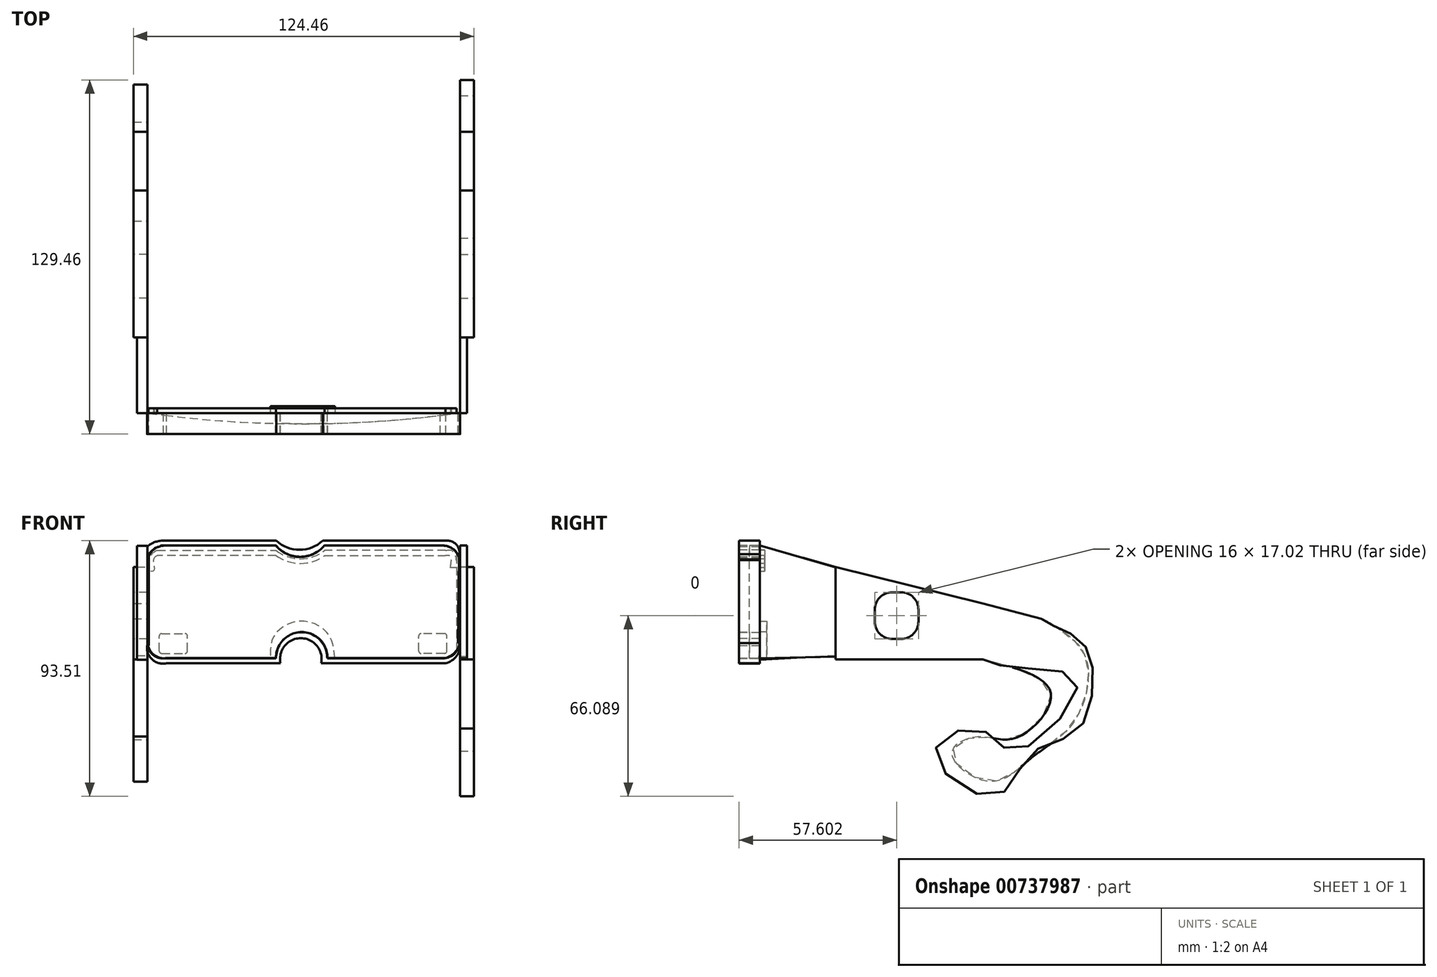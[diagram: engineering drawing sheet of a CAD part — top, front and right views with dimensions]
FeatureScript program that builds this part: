
annotation { "Feature Type Name" : "Feature", "Feature Type Description" : "" }
export const myFeature = defineFeature(function(context is Context, id is Id, definition is map)
    precondition{}
    {
        {
            var Q0;
            Q0=qCreatedBy(makeId("Front.planeOp"),FACE);
            var sketch = newSketch(context, id + "F0", { "sketchPlane" : qUnion([Q0])});
            skLineSegment(sketch, "E0", {"start": v(0, 0) * mm, "end": v(-56.1, 0) * mm});
            skLineSegment(sketch, "E1.left", {"start": v(-56.1, 21.29) * mm, "end": v(-56.1, -7.3) * mm});
            skLineSegment(sketch, "E1.right", {"start": v(58.2, 21.29) * mm, "end": v(58.2, -7.3) * mm});
            skArc(sketch, "E2", {"start": v(9.78, -13.65) * mm, "mid": v(0.38, -3.97) * mm, "end": v(-9.02, -13.65) * mm});
            skArc(sketch, "E3", {"start": v(-9.02, 27.64) * mm, "mid": v(-0.21, 23.55) * mm, "end": v(8.59, 27.64) * mm});
            skLineSegment(sketch, "E4", {"start": v(-9.02, 27.64) * mm, "end": v(-49.75, 27.64) * mm});
            skLineSegment(sketch, "E5", {"start": v(8.59, 27.64) * mm, "end": v(51.85, 27.64) * mm});
            skPoint(sketch, "E6.visualSharp", {"position": v(58.2, 27.64) * mm});
            skArc(sketch, "E6.filletArc", {"start": v(58.2, 21.29) * mm, "mid": v(56.34, 25.78) * mm, "end": v(51.85, 27.64) * mm});
            skPoint(sketch, "E7.visualSharp", {"position": v(-56.1, -13.65) * mm});
            skArc(sketch, "E7.filletArc", {"start": v(-56.1, -7.3) * mm, "mid": v(-54.24, -11.79) * mm, "end": v(-49.75, -13.65) * mm});
            skPoint(sketch, "E8.visualSharp", {"position": v(58.2, -13.65) * mm});
            skArc(sketch, "E8.filletArc", {"start": v(51.85, -13.65) * mm, "mid": v(56.34, -11.79) * mm, "end": v(58.2, -7.3) * mm});
            skPoint(sketch, "E9.visualSharp", {"position": v(-56.1, 27.64) * mm});
            skArc(sketch, "E9.filletArc", {"start": v(-49.75, 27.64) * mm, "mid": v(-54.24, 25.78) * mm, "end": v(-56.1, 21.29) * mm});
            skLineSegment(sketch, "E10", {"start": v(-49.75, -13.65) * mm, "end": v(-9.02, -13.65) * mm});
            skLineSegment(sketch, "E11", {"start": v(9.78, -13.65) * mm, "end": v(51.85, -13.65) * mm});
            skSolve(sketch);
        }
        {
            var Q0;
            Q0 = qSketchRegion(id + "F0", true);
            extrude(context, id + "F1", {"entities" : qUnion([Q0]), "depth" : 7.62 * mm, "offsetDistance" : 25.4 * mm});
        }
        {
            var Q0;
            Q0=makeQuery(id+"F1.opExtrude","SWEPT_FACE",FACE,{"disambiguationData":[OSD([sQuery(id+"F0.wireOp",EDGE,"E1.left")])]});
            var sketch = newSketch(context, id + "F2", { "sketchPlane" : qUnion([Q0])});
            skLineSegment(sketch, "E12", {"start": v(-81.46, 6.5) * mm, "end": v(-102.82, 0.93) * mm});
            skLineSegment(sketch, "E13", {"start": v(-81.46, 6.5) * mm, "end": v(-27.72, 19.8) * mm});
            skLineSegment(sketch, "E14", {"start": v(-27.72, 19.8) * mm, "end": v(-27.72, -13.96) * mm});
            skLineSegment(sketch, "E15", {"start": v(-27.72, -13.96) * mm, "end": v(-81.46, -13.96) * mm});
            skFitSpline(sketch, "E16", {"points": [v(-102.82, 0.93) * mm, v(-116.05, -8.24) * mm, v(-120.11, -19.54) * mm, v(-114, -37.86) * mm, v(-99.08, -50.15) * mm, v(-84.07, -58.64) * mm, v(-70.26, -48.38) * mm, v(-79.62, -42.2) * mm, v(-93.48, -42.69) * mm, v(-106.42, -26.64) * mm, v(-81.46, -13.96) * mm], "startDerivative": vector(-156.2, -86.96) * mm, "endDerivative": vector(283.77, 71.45) * mm});
            skSolve(sketch);
        }
        {
            var Q0;
            Q0=makeQuery(id+"F1.opExtrude","SWEPT_FACE",FACE,{"disambiguationData":[OSD([sQuery(id+"F0.wireOp",EDGE,"E1.right")])]});
            var sketch = newSketch(context, id + "F3", { "sketchPlane" : qUnion([Q0])});
            skLineSegment(sketch, "E17.0", {"start": v(81.46, 6.5) * mm, "end": v(102.82, 0.93) * mm});
            skLineSegment(sketch, "E18.0", {"start": v(81.46, 6.5) * mm, "end": v(27.72, 19.8) * mm});
            skLineSegment(sketch, "E19.0", {"start": v(27.72, -13.96) * mm, "end": v(81.46, -13.96) * mm});
            skLineSegment(sketch, "E20.0", {"start": v(27.72, 19.8) * mm, "end": v(27.72, -13.96) * mm});
            skFitSpline(sketch, "E21.0", {"points": [v(102.82, 0.93) * mm, v(107.86, -1.87) * mm, v(117.25, -7.1) * mm, v(121.8, -19.57) * mm, v(115.86, -40.05) * mm, v(98.69, -48.83) * mm, v(85.88, -63.95) * mm, v(64, -48.06) * mm, v(80.86, -39.67) * mm, v(93.38, -47.41) * mm, v(115.95, -22.64) * mm, v(93.53, -17) * mm, v(81.46, -13.96) * mm]});
            skSolve(sketch);
        }
        {
            var Q0;
            Q0=makeQuery(id+"F1.opExtrude","CAP_FACE",FACE,{"disambiguationData":[OSD([sQuery(id+"F0.wireOp",EDGE,"E1.left"),sQuery(id+"F0.wireOp",EDGE,"E1.right"),sQuery(id+"F0.wireOp",EDGE,"E2"),sQuery(id+"F0.wireOp",EDGE,"E3"),sQuery(id+"F0.wireOp",EDGE,"E4"),sQuery(id+"F0.wireOp",EDGE,"E5"),sQuery(id+"F0.wireOp",EDGE,"E6.filletArc"),sQuery(id+"F0.wireOp",EDGE,"E7.filletArc"),sQuery(id+"F0.wireOp",EDGE,"E8.filletArc"),sQuery(id+"F0.wireOp",EDGE,"E9.filletArc"),sQuery(id+"F0.wireOp",EDGE,"E10"),sQuery(id+"F0.wireOp",EDGE,"E11")])],"isStart":true});
            var sketch = newSketch(context, id + "F4", { "sketchPlane" : qUnion([Q0])});
            skFitSpline(sketch, "E22", {"points": [v(-12.46, -13.65) * mm, v(-9.95, -4.63) * mm, v(0, 0) * mm, v(9.63, -5.17) * mm, v(11.07, -13.65) * mm], "startDerivative": vector(3.74, 39.95) * mm, "endDerivative": vector(-1, -38.53) * mm});
            skLineSegment(sketch, "E23", {"start": v(-12.46, -13.65) * mm, "end": v(-9.78, -13.65) * mm});
            skArc(sketch, "E24", {"start": v(9.02, -13.65) * mm, "mid": v(-0.38, -3.9) * mm, "end": v(-9.78, -13.65) * mm});
            skLineSegment(sketch, "E25", {"start": v(9.02, -13.65) * mm, "end": v(11.07, -13.65) * mm});
            skLineSegment(sketch, "E26", {"start": v(-9.78, -13.65) * mm, "end": v(-12.46, -13.65) * mm});
            skSolve(sketch);
        }
        {
            var Q0;
            {var subQ0=sQuery(id+"F4.wireOp",EDGE,"E22");Q0=makeQuery(id+"F4.imprint","IMPRINT",FACE,{"disambiguationData":[TD([[makeQuery(id+"F4.imprint","IMPRINT",EDGE,{"derivedFrom":subQ0}),-1.0]])]});}
            extrude(context, id + "F5", {"entities" : qUnion([Q0]), "depth" : 2.54 * mm, "offsetDistance" : 25.4 * mm});
        }
        {
            var Q0;
            Q0=makeQuery(id+"F1.opExtrude","CAP_FACE",FACE,{"disambiguationData":[OSD([sQuery(id+"F0.wireOp",EDGE,"E1.left"),sQuery(id+"F0.wireOp",EDGE,"E1.right"),sQuery(id+"F0.wireOp",EDGE,"E2"),sQuery(id+"F0.wireOp",EDGE,"E3"),sQuery(id+"F0.wireOp",EDGE,"E4"),sQuery(id+"F0.wireOp",EDGE,"E5"),sQuery(id+"F0.wireOp",EDGE,"E6.filletArc"),sQuery(id+"F0.wireOp",EDGE,"E7.filletArc"),sQuery(id+"F0.wireOp",EDGE,"E8.filletArc"),sQuery(id+"F0.wireOp",EDGE,"E9.filletArc"),sQuery(id+"F0.wireOp",EDGE,"E10"),sQuery(id+"F0.wireOp",EDGE,"E11")])],"isStart":true});
            var sketch = newSketch(context, id + "F6", { "sketchPlane" : qUnion([Q0])});
            skPoint(sketch, "E27.firstSnap0", {"position": v(54.24, -11.79) * mm});
            skLineSegment(sketch, "E27.bottom", {"start": v(50.85, -11.79) * mm, "end": v(42.32, -11.79) * mm});
            skLineSegment(sketch, "E27.top", {"start": v(50.85, -4.55) * mm, "end": v(42.32, -4.55) * mm});
            skLineSegment(sketch, "E27.left", {"start": v(51.72, -10.92) * mm, "end": v(51.72, -5.42) * mm});
            skLineSegment(sketch, "E27.right", {"start": v(41.45, -10.92) * mm, "end": v(41.45, -5.42) * mm});
            skLineSegment(sketch, "E28.bottom", {"start": v(-52.52, -11.79) * mm, "end": v(-44, -11.79) * mm});
            skLineSegment(sketch, "E28.top", {"start": v(-52.52, -4.55) * mm, "end": v(-44, -4.55) * mm});
            skLineSegment(sketch, "E28.left", {"start": v(-53.4, -10.92) * mm, "end": v(-53.4, -5.42) * mm});
            skLineSegment(sketch, "E28.right", {"start": v(-43.12, -10.92) * mm, "end": v(-43.12, -5.42) * mm});
            skPoint(sketch, "E29.visualSharp", {"position": v(-53.4, -4.55) * mm});
            skArc(sketch, "E29.filletArc", {"start": v(-52.52, -4.55) * mm, "mid": v(-53.14, -4.8) * mm, "end": v(-53.4, -5.42) * mm});
            skPoint(sketch, "E30.visualSharp", {"position": v(-43.12, -4.55) * mm});
            skArc(sketch, "E30.filletArc", {"start": v(-43.12, -5.42) * mm, "mid": v(-43.38, -4.8) * mm, "end": v(-44, -4.55) * mm});
            skPoint(sketch, "E31.visualSharp", {"position": v(-43.12, -11.79) * mm});
            skArc(sketch, "E31.filletArc", {"start": v(-44, -11.79) * mm, "mid": v(-43.38, -11.53) * mm, "end": v(-43.12, -10.92) * mm});
            skPoint(sketch, "E32.visualSharp", {"position": v(-53.4, -11.79) * mm});
            skArc(sketch, "E32.filletArc", {"start": v(-53.4, -10.92) * mm, "mid": v(-53.14, -11.53) * mm, "end": v(-52.52, -11.79) * mm});
            skPoint(sketch, "E33.visualSharp", {"position": v(41.45, -4.55) * mm});
            skArc(sketch, "E33.filletArc", {"start": v(42.32, -4.55) * mm, "mid": v(41.7, -4.8) * mm, "end": v(41.45, -5.42) * mm});
            skPoint(sketch, "E34.visualSharp", {"position": v(51.72, -4.55) * mm});
            skArc(sketch, "E34.filletArc", {"start": v(51.72, -5.42) * mm, "mid": v(51.47, -4.8) * mm, "end": v(50.85, -4.55) * mm});
            skPoint(sketch, "E35.visualSharp", {"position": v(51.72, -11.79) * mm});
            skArc(sketch, "E35.filletArc", {"start": v(50.85, -11.79) * mm, "mid": v(51.47, -11.53) * mm, "end": v(51.72, -10.92) * mm});
            skPoint(sketch, "E36.visualSharp", {"position": v(41.45, -11.79) * mm});
            skArc(sketch, "E36.filletArc", {"start": v(41.45, -10.92) * mm, "mid": v(41.7, -11.53) * mm, "end": v(42.32, -11.79) * mm});
            skSolve(sketch);
        }
        {
            var Q0;
            Q0 = qSketchRegion(id + "F6", true);
            extrude(context, id + "F7", {"entities" : qUnion([Q0]), "depth" : 0.03 * mm, "offsetDistance" : 25.4 * mm});
        }
        {
            var Q0;
            {var subQ0=sQuery(id+"F0.wireOp",EDGE,"E1.left");Q0=makeQuery(id+"F2.imprint","IMPRINT",FACE,{"disambiguationData":[TD([[makeQuery(id+"F2.imprint","IMPRINT",EDGE,{"derivedFrom":makeQuery(id+"F1.opExtrude","CAP_EDGE",EDGE,{"disambiguationData":[OSD([subQ0])],"isStart":true})}),1.0]])]});}
            var sketch = newSketch(context, id + "F8", { "sketchPlane" : qUnion([Q0])});
            skLineSegment(sketch, "E37", {"start": v(0, 27.59) * mm, "end": v(-27.72, 19.8) * mm});
            skLineSegment(sketch, "E38", {"start": v(-27.72, 19.8) * mm, "end": v(-27.72, -12.59) * mm});
            skLineSegment(sketch, "E39", {"start": v(-27.72, -12.59) * mm, "end": v(0, -14.06) * mm});
            skLineSegment(sketch, "E40", {"start": v(0, -14.06) * mm, "end": v(0, 27.59) * mm});
            skSolve(sketch);
        }
        {
            var Q0;
            {var subQ4=sQuery(id+"F8.wireOp",EDGE,"E37");Q0=makeQuery(id+"F8.imprint","IMPRINT",FACE,{"disambiguationData":[TD([[makeQuery(id+"F8.imprint","IMPRINT",EDGE,{"derivedFrom":subQ4}),1.0]])]});}
            extrude(context, id + "F9", {"entities" : qUnion([Q0]), "depth" : 3.8 * mm, "offsetDistance" : 25.4 * mm});
        }
        {
            var Q0;
            {var subQ0=sQuery(id+"F0.wireOp",EDGE,"E1.right");Q0=makeQuery(id+"F3.imprint","IMPRINT",FACE,{"disambiguationData":[TD([[makeQuery(id+"F3.imprint","IMPRINT",EDGE,{"derivedFrom":makeQuery(id+"F1.opExtrude","CAP_EDGE",EDGE,{"disambiguationData":[OSD([subQ0])],"isStart":true})}),-1.0]])]});}
            var sketch = newSketch(context, id + "F10", { "sketchPlane" : qUnion([Q0])});
            skLineSegment(sketch, "E41", {"start": v(0, 27.68) * mm, "end": v(27.8, 19.72) * mm});
            skLineSegment(sketch, "E42", {"start": v(27.8, 19.72) * mm, "end": v(27.8, -12.92) * mm});
            skLineSegment(sketch, "E43", {"start": v(27.8, -12.92) * mm, "end": v(0, -13.63) * mm});
            skLineSegment(sketch, "E44", {"start": v(0, -13.63) * mm, "end": v(0, 27.68) * mm});
            skSolve(sketch);
        }
        {
            var Q0;
            Q0 = qSketchRegion(id + "F10", true);
            extrude(context, id + "F11", {"entities" : qUnion([Q0]), "operationType" : NewBodyOperationType.ADD, "depth" : 2.54 * mm, "offsetDistance" : 25.4 * mm});
        }
        {
            var Q0;
            Q0 = qSketchRegion(id + "F2", true);
            extrude(context, id + "F12", {"entities" : qUnion([Q0]), "depth" : 5.08 * mm, "offsetDistance" : 25.4 * mm});
        }
        {
            var Q0;
            Q0=makeQuery(id+"F3.imprint","IMPRINT",FACE,{"disambiguationData":[TD([[makeQuery(id+"F3.imprint","IMPRINT",EDGE,{"derivedFrom":sQuery(id+"F3.wireOp",EDGE,"E17.0")}),-1.0]])]});
            extrude(context, id + "F13", {"entities" : qUnion([Q0]), "depth" : 5.08 * mm, "offsetDistance" : 25.4 * mm});
        }
        {
            var Q0;
            Q0=makeQuery(id+"F1.opExtrude","CAP_FACE",FACE,{"disambiguationData":[OSD([sQuery(id+"F0.wireOp",EDGE,"E1.left"),sQuery(id+"F0.wireOp",EDGE,"E1.right"),sQuery(id+"F0.wireOp",EDGE,"E2"),sQuery(id+"F0.wireOp",EDGE,"E3"),sQuery(id+"F0.wireOp",EDGE,"E4"),sQuery(id+"F0.wireOp",EDGE,"E5"),sQuery(id+"F0.wireOp",EDGE,"E6.filletArc"),sQuery(id+"F0.wireOp",EDGE,"E7.filletArc"),sQuery(id+"F0.wireOp",EDGE,"E8.filletArc"),sQuery(id+"F0.wireOp",EDGE,"E9.filletArc"),sQuery(id+"F0.wireOp",EDGE,"E10"),sQuery(id+"F0.wireOp",EDGE,"E11")])],"isStart":true});
            var sketch = newSketch(context, id + "F14", { "sketchPlane" : qUnion([Q0])});
            skLineSegment(sketch, "E45", {"start": v(-52.96, 25.9) * mm, "end": v(-8.76, 25.9) * mm});
            skLineSegment(sketch, "E46", {"start": v(-8.76, 24) * mm, "end": v(-52.96, 24) * mm});
            skLineSegment(sketch, "E47", {"start": v(9.02, 24) * mm, "end": v(52.45, 24) * mm});
            skLineSegment(sketch, "E48", {"start": v(52.45, 25.9) * mm, "end": v(9.02, 25.9) * mm});
            skFitSpline(sketch, "E49", {"points": [v(52.45, 25.9) * mm, v(53.93, 25.01) * mm, v(55.17, 23.4) * mm, v(55.21, 18.5) * mm, v(53.61, 18.6) * mm, v(53.61, 20.64) * mm, v(53.61, 23.1) * mm, v(52.45, 24) * mm], "startDerivative": vector(12.2, -6.9) * mm, "endDerivative": vector(-12.05, 5.82) * mm});
            skFitSpline(sketch, "E50", {"points": [v(-52.96, 25.9) * mm, v(-55.12, 25.9) * mm, v(-56.25, 24.48) * mm, v(-56.93, 21.54) * mm, v(-56.86, 19.5) * mm], "startDerivative": vector(-9.7, 1.47) * mm, "endDerivative": vector(0.84, -7.98) * mm});
            skArc(sketch, "E51", {"start": v(-8.76, 25.9) * mm, "mid": v(0.13, 22.77) * mm, "end": v(9.02, 25.9) * mm});
            skArc(sketch, "E52", {"start": v(-8.76, 24) * mm, "mid": v(0.13, 21.13) * mm, "end": v(9.02, 24) * mm});
            skLineSegment(sketch, "E53", {"start": v(-56.86, 19.5) * mm, "end": v(-54.7, 19.5) * mm});
            skFitSpline(sketch, "E54", {"points": [v(-54.7, 19.5) * mm, v(-54.7, 23.67) * mm, v(-52.96, 24) * mm], "startDerivative": vector(-1.33, 8.72) * mm, "endDerivative": vector(5.26, -0.36) * mm});
            skSolve(sketch);
        }
        {
            var Q0;
            Q0 = qSketchRegion(id + "F14", true);
            extrude(context, id + "F15", {"entities" : qUnion([Q0]), "depth" : 1.78 * mm, "offsetDistance" : 25.4 * mm});
        }
        {
            var Q0;
            Q0=makeQuery(id+"F12.opExtrude","CAP_FACE",FACE,{"disambiguationData":[OSD([sQuery(id+"F2.wireOp",EDGE,"E12"),sQuery(id+"F2.wireOp",EDGE,"tiHaeCkr-vmON-xEy8-UvQG-xXYS2zljbIE3"),sQuery(id+"F2.wireOp",EDGE,"TNWGmv4X-bEus-kIfE-oV3Z-ihmAzDLnALsF"),sQuery(id+"F2.wireOp",EDGE,"c96oVTAL-4Pca-aYuN-eGpR-bl0jGNkDnoI0"),sQuery(id+"F2.wireOp",EDGE,"kEhlCoJh-upeX-Yck7-pCzs-ke9frVV1XHoU"),sQuery(id+"F2.wireOp",EDGE,"TjoAkAm7-V7CV-dwsU-kwPn-YouIpEai78Xo"),sQuery(id+"F2.wireOp",EDGE,"9CvSjDup-Y4bS-zvld-aLKK-vra1aofiwF2Y"),sQuery(id+"F2.wireOp",EDGE,"7ubKDvWw-GHld-qY0L-6730-EqHYWj8qa3FC"),sQuery(id+"F2.wireOp",EDGE,"E13"),sQuery(id+"F2.wireOp",EDGE,"E14"),sQuery(id+"F2.wireOp",EDGE,"E15")])],"isStart":false});
            var sketch = newSketch(context, id + "F16", { "sketchPlane" : qUnion([Q0])});
            skLineSegment(sketch, "E55", {"start": v(-41.98, 4.19) * mm, "end": v(-41.98, -0.13) * mm});
            skLineSegment(sketch, "E56", {"start": v(-48.33, -6.48) * mm, "end": v(-51.63, -6.48) * mm});
            skLineSegment(sketch, "E57", {"start": v(-57.98, -0.13) * mm, "end": v(-57.98, 4.19) * mm});
            skLineSegment(sketch, "E58", {"start": v(-51.63, 10.54) * mm, "end": v(-48.33, 10.54) * mm});
            skPoint(sketch, "E59.visualSharp", {"position": v(-57.98, 10.54) * mm});
            skArc(sketch, "E59.filletArc", {"start": v(-51.63, 10.54) * mm, "mid": v(-56.12, 8.68) * mm, "end": v(-57.98, 4.19) * mm});
            skPoint(sketch, "E60.visualSharp", {"position": v(-41.98, 10.54) * mm});
            skArc(sketch, "E60.filletArc", {"start": v(-41.98, 4.19) * mm, "mid": v(-43.84, 8.68) * mm, "end": v(-48.33, 10.54) * mm});
            skPoint(sketch, "E61.visualSharp", {"position": v(-41.98, -6.48) * mm});
            skArc(sketch, "E61.filletArc", {"start": v(-48.33, -6.48) * mm, "mid": v(-43.84, -4.62) * mm, "end": v(-41.98, -0.13) * mm});
            skPoint(sketch, "E62.visualSharp", {"position": v(-57.98, -6.48) * mm});
            skArc(sketch, "E62.filletArc", {"start": v(-57.98, -0.13) * mm, "mid": v(-56.12, -4.62) * mm, "end": v(-51.63, -6.48) * mm});
            skSolve(sketch);
        }
        {
            var Q0;
            Q0 = qSketchRegion(id + "F16", true);
            extrude(context, id + "F17", {"entities" : qUnion([Q0]), "operationType" : NewBodyOperationType.REMOVE, "oppositeDirection" : true, "depth" : 25.4 * mm, "offsetDistance" : 25.4 * mm});
        }
        {
            var Q0;
            Q0=makeQuery(id+"F13.opExtrude","CAP_FACE",FACE,{"disambiguationData":[OSD([sQuery(id+"F3.wireOp",EDGE,"E17.0"),sQuery(id+"F3.wireOp",EDGE,"3026987a-cd17-47ce-957c-b74f86dfe605.0"),sQuery(id+"F3.wireOp",EDGE,"39190db7-4cbc-4524-aeab-41a107a8df5b.0"),sQuery(id+"F3.wireOp",EDGE,"1a617bd4-6713-4560-a2fb-f82e55d89a12.0"),sQuery(id+"F3.wireOp",EDGE,"a00d29ea-d03a-4b99-beb4-be851129cc69.0"),sQuery(id+"F3.wireOp",EDGE,"9b353753-5025-420e-9f11-0bb499617e29.0"),sQuery(id+"F3.wireOp",EDGE,"b30b721c-cf88-40e2-9981-8eac7387f709.0"),sQuery(id+"F3.wireOp",EDGE,"b0ce85b5-cade-4131-82d7-5940075cd0e0.0"),sQuery(id+"F3.wireOp",EDGE,"E18.0"),sQuery(id+"F3.wireOp",EDGE,"E19.0"),sQuery(id+"F3.wireOp",EDGE,"E20.0")])],"isStart":false});
            var sketch = newSketch(context, id + "F18", { "sketchPlane" : qUnion([Q0])});
            skArc(sketch, "E63.0", {"start": v(41.98, 4.19) * mm, "mid": v(43.84, 8.68) * mm, "end": v(48.33, 10.54) * mm});
            skArc(sketch, "E64.0", {"start": v(51.63, 10.54) * mm, "mid": v(56.12, 8.68) * mm, "end": v(57.98, 4.19) * mm});
            skLineSegment(sketch, "E65.0", {"start": v(57.98, -0.13) * mm, "end": v(57.98, 4.19) * mm});
            skArc(sketch, "E66.0", {"start": v(57.98, -0.13) * mm, "mid": v(56.12, -4.62) * mm, "end": v(51.63, -6.48) * mm});
            skLineSegment(sketch, "E67.0", {"start": v(41.98, 4.19) * mm, "end": v(41.98, -0.13) * mm});
            skArc(sketch, "E68.0", {"start": v(48.33, -6.48) * mm, "mid": v(43.84, -4.62) * mm, "end": v(41.98, -0.13) * mm});
            skLineSegment(sketch, "E69.0", {"start": v(48.33, -6.48) * mm, "end": v(51.63, -6.48) * mm});
            skLineSegment(sketch, "E70.0", {"start": v(51.63, 10.54) * mm, "end": v(48.33, 10.54) * mm});
            skSolve(sketch);
        }
        {
            var Q0;
            Q0 = qSketchRegion(id + "F18", true);
            extrude(context, id + "F19", {"entities" : qUnion([Q0]), "operationType" : NewBodyOperationType.REMOVE, "oppositeDirection" : true, "depth" : 25.4 * mm, "offsetDistance" : 25.4 * mm});
        }
        {
            var Q0;
            Q0=makeQuery(id+"F1.opExtrude","SWEPT_FACE",FACE,{"disambiguationData":[OSD([sQuery(id+"F0.wireOp",EDGE,"E4")])]});
            var sketch = newSketch(context, id + "F20", { "sketchPlane" : qUnion([Q0])});
            skArc(sketch, "E71", {"start": v(-55.58, 0) * mm, "mid": v(0.78, -3.9) * mm, "end": v(57.14, 0) * mm});
            skLineSegment(sketch, "E72", {"start": v(-55.58, 0) * mm, "end": v(57.14, 0) * mm});
            skSolve(sketch);
        }
        {
            var Q0;
            Q0 = qSketchRegion(id + "F20", true);
            extrude(context, id + "F21", {"entities" : qUnion([Q0]), "operationType" : NewBodyOperationType.REMOVE, "endBound" : BoundingType.THROUGH_ALL, "oppositeDirection" : true, "depth" : 25.4 * mm, "offsetDistance" : 25.4 * mm});
        }
        {
            var Q0;
            Q0=qCreatedBy(makeId("Front.planeOp"),FACE);
            var sketch = newSketch(context, id + "F22", { "sketchPlane" : qUnion([Q0])});
            skLineSegment(sketch, "E73", {"start": v(-50.25, 29.45) * mm, "end": v(-8.94, 29.45) * mm});
            skArc(sketch, "E74", {"start": v(-8.94, 29.45) * mm, "mid": v(-0.46, 26.1) * mm, "end": v(8.01, 29.45) * mm});
            skLineSegment(sketch, "E75", {"start": v(8.01, 29.45) * mm, "end": v(53.66, 29.45) * mm});
            skArc(sketch, "E76", {"start": v(57.82, 26.23) * mm, "mid": v(56.3, 28.55) * mm, "end": v(53.66, 29.45) * mm});
            skLineSegment(sketch, "E77", {"start": v(57.82, 26.23) * mm, "end": v(58.27, 24.51) * mm});
            skLineSegment(sketch, "E78", {"start": v(58.27, 24.51) * mm, "end": v(58.27, 22.34) * mm});
            skLineSegment(sketch, "E79", {"start": v(58.27, 22.34) * mm, "end": v(58.22, 22.88) * mm});
            skFitSpline(sketch, "E80", {"points": [v(58.27, 22.34) * mm, v(58.22, 22.88) * mm, v(57.3, 24.51) * mm, v(56.67, 25.48) * mm, v(55.74, 26.35) * mm, v(54.64, 26.98) * mm, v(53.1, 27.55) * mm, v(51.03, 27.65) * mm], "startDerivative": vector(0.38, 5.15) * mm, "endDerivative": vector(-12.14, -0.25) * mm});
            skLineSegment(sketch, "E81", {"start": v(51.03, 27.65) * mm, "end": v(8.6, 27.65) * mm});
            skArc(sketch, "E82", {"start": v(-9.15, 27.68) * mm, "mid": v(-0.28, 23.45) * mm, "end": v(8.6, 27.65) * mm});
            skLineSegment(sketch, "E83", {"start": v(-9.7, 27.68) * mm, "end": v(-50.25, 27.68) * mm});
            skFitSpline(sketch, "E84", {"points": [v(-50.25, 27.68) * mm, v(-50.82, 27.68) * mm, v(-51.82, 27.2) * mm, v(-53.15, 26.8) * mm, v(-54.36, 25.8) * mm, v(-55.36, 24.73) * mm, v(-56.1, 22.26) * mm], "startDerivative": vector(-5.12, 0.82) * mm, "endDerivative": vector(-2.48, -12.3) * mm});
            skLineSegment(sketch, "E85", {"start": v(-56.1, 22.26) * mm, "end": v(-56.1, 27.34) * mm});
            skArc(sketch, "E86", {"start": v(-50.25, 29.45) * mm, "mid": v(-53.35, 28.9) * mm, "end": v(-56.1, 27.34) * mm});
            skLineSegment(sketch, "E87", {"start": v(-9.7, 27.68) * mm, "end": v(-9.15, 27.68) * mm});
            skSolve(sketch);
        }
        {
            var Q0;
            Q0 = qSketchRegion(id + "F22", true);
            extrude(context, id + "F23", {"entities" : qUnion([Q0]), "depth" : 7.62 * mm, "offsetDistance" : 25.4 * mm});
        }
        {
            var Q0;
            Q0=qCreatedBy(makeId("Front.planeOp"),FACE);
            var sketch = newSketch(context, id + "F24", { "sketchPlane" : qUnion([Q0])});
            skLineSegment(sketch, "E88", {"start": v(-56.13, -8.91) * mm, "end": v(-55.56, -8.91) * mm});
            skLineSegment(sketch, "E89", {"start": v(-56.11, 22.56) * mm, "end": v(-56.13, -8.91) * mm});
            skLineSegment(sketch, "E90", {"start": v(-55.56, -8.91) * mm, "end": v(-55.56, 24.33) * mm});
            skLineSegment(sketch, "E91", {"start": v(-55.56, 24.33) * mm, "end": v(-56.11, 22.56) * mm});
            skSolve(sketch);
        }
        {
            var Q0;
            Q0 = qSketchRegion(id + "F24", true);
            extrude(context, id + "F25", {"entities" : qUnion([Q0]), "depth" : 7.62 * mm, "offsetDistance" : 25.4 * mm});
        }
        {
            var Q0;
            Q0=qCreatedBy(makeId("Front.planeOp"),FACE);
            var sketch = newSketch(context, id + "F26", { "sketchPlane" : qUnion([Q0])});
            skLineSegment(sketch, "E92", {"start": v(58.19, 23.02) * mm, "end": v(58.19, -7.98) * mm});
            skLineSegment(sketch, "E93", {"start": v(58.19, -7.98) * mm, "end": v(57.5, -7.98) * mm});
            skLineSegment(sketch, "E94", {"start": v(57.5, -7.98) * mm, "end": v(57.87, 23.61) * mm});
            skLineSegment(sketch, "E95", {"start": v(57.87, 23.61) * mm, "end": v(58.19, 23.02) * mm});
            skSolve(sketch);
        }
        {
            var Q0;
            Q0 = qSketchRegion(id + "F26", true);
            extrude(context, id + "F27", {"entities" : qUnion([Q0]), "depth" : 7.62 * mm, "offsetDistance" : 25.4 * mm});
        }
        {
            var Q0;
            Q0=qCreatedBy(makeId("Front.planeOp"),FACE);
            var sketch = newSketch(context, id + "F28", { "sketchPlane" : qUnion([Q0])});
            skLineSegment(sketch, "E96", {"start": v(-49.1, -15.4) * mm, "end": v(-7.4, -15.4) * mm});
            skArc(sketch, "E97", {"start": v(7.44, -15.4) * mm, "mid": v(0.02, -6.21) * mm, "end": v(-7.4, -15.4) * mm});
            skLineSegment(sketch, "E98", {"start": v(7.44, -15.4) * mm, "end": v(52.97, -15.4) * mm});
            skLineSegment(sketch, "E99", {"start": v(-49.1, -13.45) * mm, "end": v(-9.07, -13.45) * mm});
            skArc(sketch, "E100", {"start": v(9.66, -13.45) * mm, "mid": v(0.3, -4.02) * mm, "end": v(-9.07, -13.45) * mm});
            skLineSegment(sketch, "E101", {"start": v(9.66, -13.45) * mm, "end": v(52.97, -13.45) * mm});
            skArc(sketch, "E102", {"start": v(52.97, -13.45) * mm, "mid": v(56.28, -11.44) * mm, "end": v(58.18, -8.06) * mm});
            skArc(sketch, "E103", {"start": v(52.97, -15.4) * mm, "mid": v(56.97, -12.72) * mm, "end": v(58.18, -8.06) * mm});
            skArc(sketch, "E104", {"start": v(-56.16, -8.92) * mm, "mid": v(-54.33, -14.01) * mm, "end": v(-49.1, -15.4) * mm});
            skArc(sketch, "E105", {"start": v(-56.16, -8.92) * mm, "mid": v(-53.57, -12.65) * mm, "end": v(-49.1, -13.45) * mm});
            skSolve(sketch);
        }
        {
            var Q0;
            Q0 = qSketchRegion(id + "F28", true);
            extrude(context, id + "F29", {"entities" : qUnion([Q0]), "depth" : 7.62 * mm, "offsetDistance" : 25.4 * mm});
        }
    });
